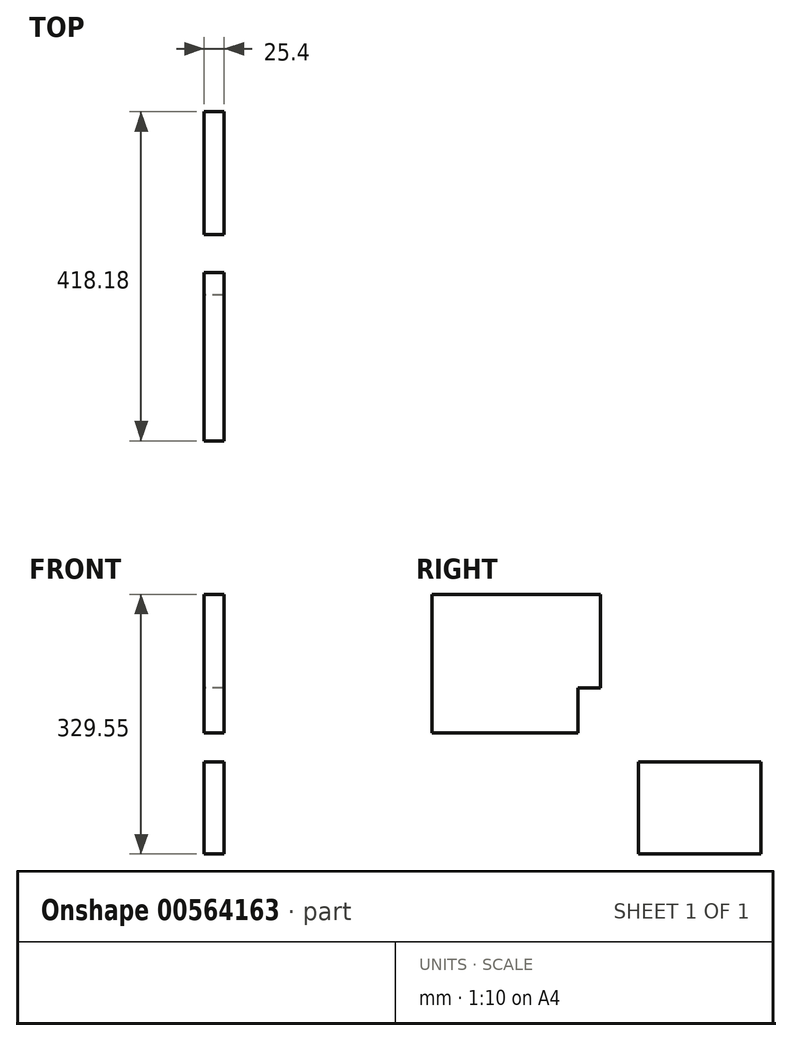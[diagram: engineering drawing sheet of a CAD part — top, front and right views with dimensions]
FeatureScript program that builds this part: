
annotation { "Feature Type Name" : "Feature", "Feature Type Description" : "" }
export const myFeature = defineFeature(function(context is Context, id is Id, definition is map)
    precondition{}
    {
        {
            var Q0;
            Q0=qCreatedBy(makeId("Right.planeOp"),FACE);
            var sketch = newSketch(context, id + "F0", { "sketchPlane" : qUnion([Q0])});
            skLineSegment(sketch, "E0.bottom", {"start": v(-57.07, 33.68) * mm, "end": v(98.97, 33.68) * mm});
            skLineSegment(sketch, "E0.top", {"start": v(-57.07, -82.95) * mm, "end": v(98.97, -82.95) * mm});
            skLineSegment(sketch, "E0.left", {"start": v(-57.07, 33.68) * mm, "end": v(-57.07, -82.95) * mm});
            skLineSegment(sketch, "E0.right", {"start": v(98.97, 33.68) * mm, "end": v(98.97, -82.95) * mm});
            skLineSegment(sketch, "E1.bottom", {"start": v(-105.21, 127.77) * mm, "end": v(-319.2, 127.77) * mm});
            skLineSegment(sketch, "E1.top", {"start": v(-105.21, 246.6) * mm, "end": v(-319.2, 246.6) * mm});
            skLineSegment(sketch, "E1.left", {"start": v(-105.21, 127.77) * mm, "end": v(-105.21, 246.6) * mm});
            skLineSegment(sketch, "E1.right", {"start": v(-319.2, 127.77) * mm, "end": v(-319.2, 246.6) * mm});
            skLineSegment(sketch, "E2.bottom", {"start": v(-319.2, 246.6) * mm, "end": v(-133.75, 246.6) * mm});
            skLineSegment(sketch, "E2.top", {"start": v(-319.2, 70.48) * mm, "end": v(-133.75, 70.48) * mm});
            skLineSegment(sketch, "E2.left", {"start": v(-319.2, 246.6) * mm, "end": v(-319.2, 70.48) * mm});
            skLineSegment(sketch, "E2.right", {"start": v(-133.75, 246.6) * mm, "end": v(-133.75, 70.48) * mm});
            skPoint(sketch, "E3.firstSnap0", {"position": v(-212.21, 127.77) * mm});
            skLineSegment(sketch, "E3.bottom", {"start": v(-212.21, 167.95) * mm, "end": v(-123.94, 167.95) * mm});
            skLineSegment(sketch, "E3.top", {"start": v(-212.21, 127.77) * mm, "end": v(-123.94, 127.77) * mm});
            skLineSegment(sketch, "E3.left", {"start": v(-212.21, 167.95) * mm, "end": v(-212.21, 127.77) * mm});
            skLineSegment(sketch, "E3.right", {"start": v(-123.94, 167.95) * mm, "end": v(-123.94, 127.77) * mm});
            skSolve(sketch);
        }
        {
            var Q0;
            Q0 = qSketchRegion(id + "F0", true);
            extrude(context, id + "F1", {"entities" : qUnion([Q0]), "depth" : 25.4 * mm, "offsetDistance" : 25.4 * mm});
        }
    });
